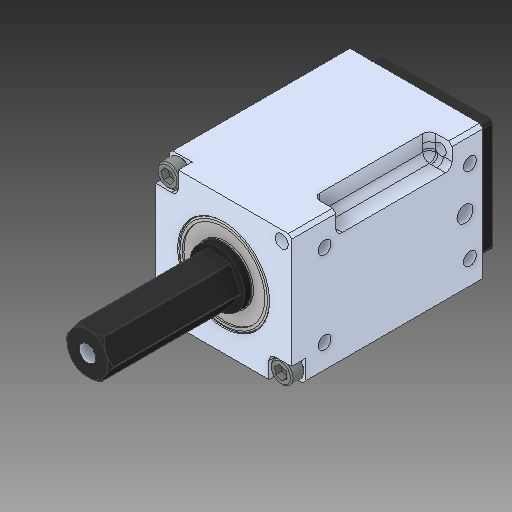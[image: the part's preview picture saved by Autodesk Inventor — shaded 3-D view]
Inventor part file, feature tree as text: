
AUTODESK INVENTOR PART (.ipt)
format: ipt  version: 2018 (Build 220112000, 112)  size: 4,146,688 bytes
history: native  units: in
note: dims shown in document units (in); Inventor stores cm internally (conversion verified against a paired STEP export)
features: other x3, sketch x1
ambient origin geometry x8: Origin, YZ Plane, XZ Plane, XY Plane, X Axis, Y Axis, Z Axis, Center Point
bodies: Solid1 (feature_tree)
feature tree (4):
  other  "VersaPlanetary_2stg_775.ipt"
  other  "Solid2::VersaPlanetary_2stg_775.ipt"
  other  "TaggingFeature1"
  sketch  "Sketch1"  dims[d0=0.3937in]
